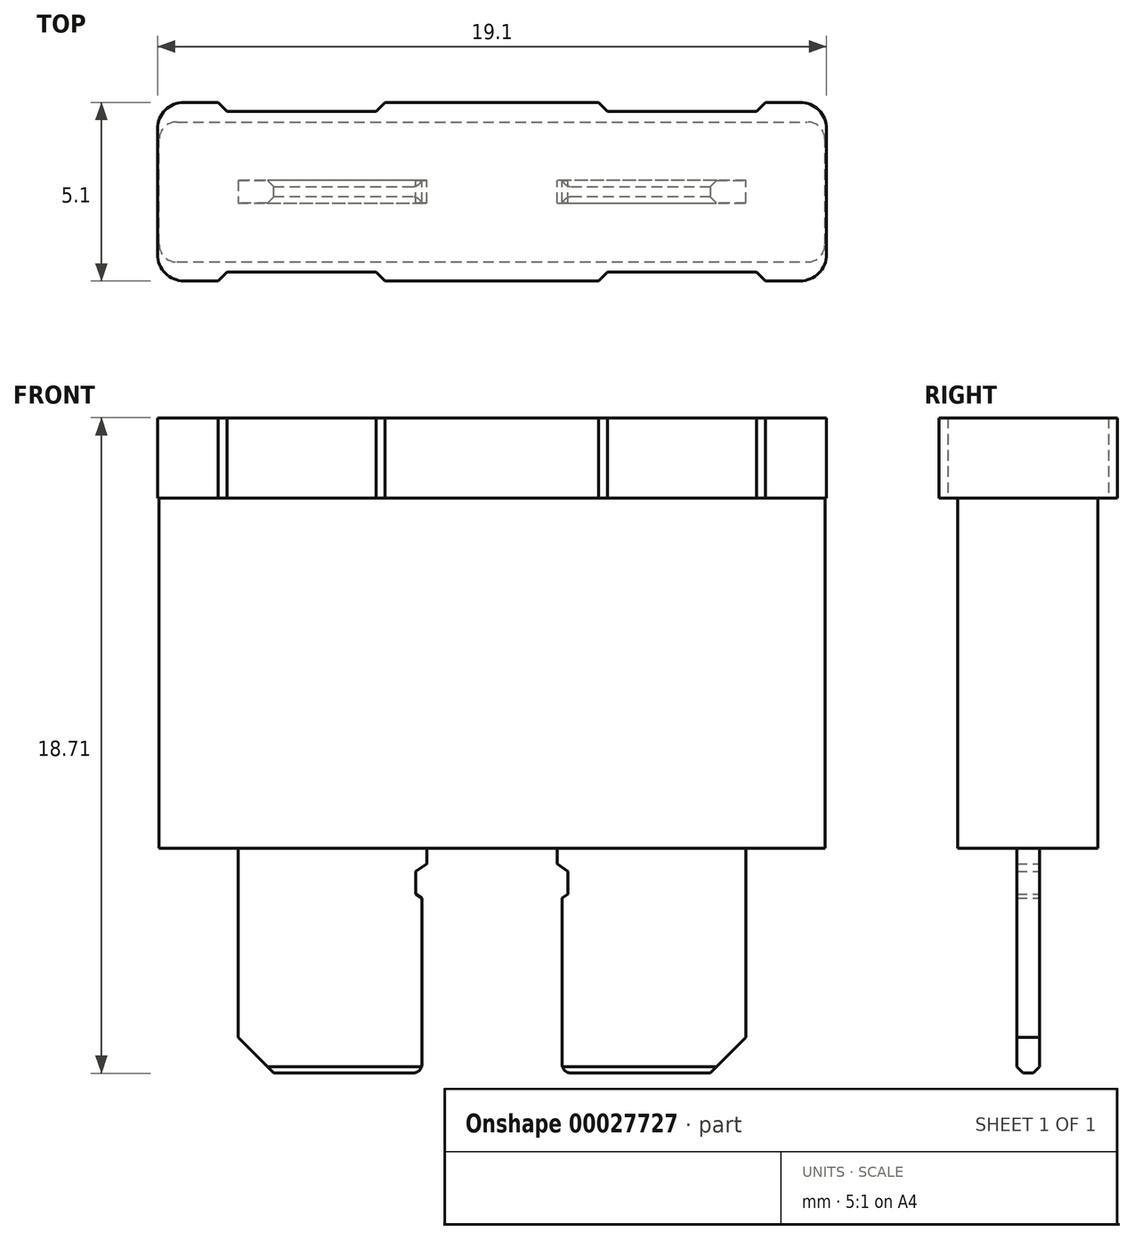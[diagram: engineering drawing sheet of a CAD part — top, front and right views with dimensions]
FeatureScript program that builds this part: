
annotation { "Feature Type Name" : "Feature", "Feature Type Description" : "" }
export const myFeature = defineFeature(function(context is Context, id is Id, definition is map)
    precondition{}
    {
        {
            var Q0;
            Q0=qCreatedBy(makeId("Top.planeOp"),FACE);
            var sketch = newSketch(context, id + "F0", { "sketchPlane" : qUnion([Q0])});
            skLineSegment(sketch, "E0.bottom", {"start": v(-8.79, -2.55) * mm, "end": v(-7.81, -2.55) * mm});
            skLineSegment(sketch, "E0.top", {"start": v(-8.79, 2.55) * mm, "end": v(-7.81, 2.55) * mm});
            skLineSegment(sketch, "E0.left", {"start": v(-9.55, -1.79) * mm, "end": v(-9.55, 1.8) * mm});
            skLineSegment(sketch, "E0.right", {"start": v(9.55, -1.79) * mm, "end": v(9.55, 1.8) * mm});
            skPoint(sketch, "E1.visualSharp", {"position": v(-9.55, 2.55) * mm});
            skArc(sketch, "E1.filletArc", {"start": v(-8.79, 2.55) * mm, "mid": v(-9.33, 2.33) * mm, "end": v(-9.55, 1.8) * mm});
            skPoint(sketch, "E2.visualSharp", {"position": v(-9.55, -2.55) * mm});
            skArc(sketch, "E2.filletArc", {"start": v(-9.55, -1.79) * mm, "mid": v(-9.33, -2.32) * mm, "end": v(-8.79, -2.55) * mm});
            skPoint(sketch, "E3.visualSharp", {"position": v(9.55, -2.55) * mm});
            skArc(sketch, "E3.filletArc", {"start": v(8.79, -2.55) * mm, "mid": v(9.33, -2.32) * mm, "end": v(9.55, -1.79) * mm});
            skPoint(sketch, "E4.visualSharp", {"position": v(9.55, 2.55) * mm});
            skArc(sketch, "E4.filletArc", {"start": v(9.55, 1.8) * mm, "mid": v(9.33, 2.33) * mm, "end": v(8.79, 2.55) * mm});
            skLineSegment(sketch, "E5.0", {"start": v(-7.81, 2.3) * mm, "end": v(-3.05, 2.3) * mm});
            skLineSegment(sketch, "E6.0", {"start": v(-7.81, -2.3) * mm, "end": v(-3.05, -2.3) * mm});
            skLineSegment(sketch, "E7", {"start": v(-3.05, 2.55) * mm, "end": v(-3.05, 2.3) * mm});
            skLineSegment(sketch, "E8", {"start": v(0, 2.55) * mm, "end": v(0, -2.55) * mm});
            skLineSegment(sketch, "E9.MirrorCS", {"start": v(3.05, 2.55) * mm, "end": v(3.05, 2.3) * mm});
            skLineSegment(sketch, "E10.0", {"start": v(-7.81, 2.55) * mm, "end": v(-7.81, 2.3) * mm});
            skLineSegment(sketch, "E11.0", {"start": v(7.81, 2.55) * mm, "end": v(7.81, 2.3) * mm});
            skLineSegment(sketch, "E12.trimOffspring", {"start": v(-3.05, 2.55) * mm, "end": v(3.05, 2.55) * mm});
            skLineSegment(sketch, "E13.trimOffspring", {"start": v(7.81, 2.55) * mm, "end": v(8.79, 2.55) * mm});
            skLineSegment(sketch, "E14.trimOffspring", {"start": v(-3.05, -2.55) * mm, "end": v(3.05, -2.55) * mm});
            skLineSegment(sketch, "E15.trimOffspring", {"start": v(7.81, -2.55) * mm, "end": v(8.79, -2.55) * mm});
            skLineSegment(sketch, "E16.trimOffspring", {"start": v(3.05, -2.3) * mm, "end": v(7.81, -2.3) * mm});
            skLineSegment(sketch, "E17.trimOffspring", {"start": v(3.05, 2.3) * mm, "end": v(7.81, 2.3) * mm});
            skLineSegment(sketch, "E18.trimOffspring", {"start": v(-3.05, -2.3) * mm, "end": v(-3.05, -2.55) * mm});
            skLineSegment(sketch, "E19.trimOffspring", {"start": v(3.05, -2.3) * mm, "end": v(3.05, -2.55) * mm});
            skLineSegment(sketch, "E20.trimOffspring", {"start": v(7.81, -2.3) * mm, "end": v(7.81, -2.55) * mm});
            skLineSegment(sketch, "E21.trimOffspring", {"start": v(-7.81, -2.3) * mm, "end": v(-7.81, -2.55) * mm});
            skSolve(sketch);
        }
        {
            var Q0;
            Q0=qSketchRegion(id+"F0",true);
            extrude(context, id + "F1", {"entities" : qUnion([Q0]), "endBound" : BoundingType.SYMMETRIC, "depth" : 2.3 * mm});
        }
        {
            var Q0;
            Q0=qCreatedBy(makeId("Right.planeOp"),FACE);
            var sketch = newSketch(context, id + "F2", { "sketchPlane" : qUnion([Q0])});
            skLineSegment(sketch, "E22.bottom", {"start": v(-2, -11.14) * mm, "end": v(2, -11.14) * mm});
            skLineSegment(sketch, "E22.top", {"start": v(-2, 0) * mm, "end": v(2, 0) * mm});
            skLineSegment(sketch, "E22.left", {"start": v(-2, -11.14) * mm, "end": v(-2, 0) * mm});
            skLineSegment(sketch, "E22.right", {"start": v(2, -11.14) * mm, "end": v(2, 0) * mm});
            skSolve(sketch);
        }
        {
            var Q0;
            Q0=qSketchRegion(id+"F2",true);
            extrude(context, id + "F3", {"entities" : qUnion([Q0]), "operationType" : NewBodyOperationType.ADD, "endBound" : BoundingType.SYMMETRIC, "depth" : 19 * mm});
        }
        {
            var Q0;
            Q0=makeQuery(id+"F3.opExtrude","CAP_EDGE",EDGE,{"disambiguationData":[OSD([sQuery(id+"F2.wireOp",EDGE,"E22.left")])],"isStart":true});
            var Q1;
            Q1=makeQuery(id+"F3.opExtrude","CAP_EDGE",EDGE,{"disambiguationData":[OSD([sQuery(id+"F2.wireOp",EDGE,"E22.right")])],"isStart":true});
            var Q2;
            Q2=makeQuery(id+"F3.opExtrude","CAP_EDGE",EDGE,{"disambiguationData":[OSD([sQuery(id+"F2.wireOp",EDGE,"E22.left")])],"isStart":false});
            var Q3;
            Q3=makeQuery(id+"F3.opExtrude","CAP_EDGE",EDGE,{"disambiguationData":[OSD([sQuery(id+"F2.wireOp",EDGE,"E22.right")])],"isStart":false});
            fillet(context, id + "F4", {"entities" : qUnion([Q0, Q1, Q2, Q3]), "radius" : 0.5 * mm, "tangentPropagation" : true, "allowEdgeOverflow" : false});
        }
        {
            var Q0;
            Q0=makeQuery(id+"F1.opExtrude","SWEPT_EDGE",EDGE,{"disambiguationData":[OSD([sQuery(id+"F0.wireOp",EDGE,"E5.0"),sQuery(id+"F0.wireOp",EDGE,"E10.0")])]});
            var Q1;
            Q1=makeQuery(id+"F1.opExtrude","SWEPT_EDGE",EDGE,{"disambiguationData":[OSD([sQuery(id+"F0.wireOp",EDGE,"E5.0"),sQuery(id+"F0.wireOp",EDGE,"E7")])]});
            var Q2;
            Q2=makeQuery(id+"F1.opExtrude","SWEPT_EDGE",EDGE,{"disambiguationData":[OSD([sQuery(id+"F0.wireOp",EDGE,"E6.0"),sQuery(id+"F0.wireOp",EDGE,"E18.trimOffspring")])]});
            var Q3;
            Q3=makeQuery(id+"F1.opExtrude","SWEPT_EDGE",EDGE,{"disambiguationData":[OSD([sQuery(id+"F0.wireOp",EDGE,"E6.0"),sQuery(id+"F0.wireOp",EDGE,"E21.trimOffspring")])]});
            var Q4;
            Q4=makeQuery(id+"F1.opExtrude","SWEPT_EDGE",EDGE,{"disambiguationData":[OSD([sQuery(id+"F0.wireOp",EDGE,"E16.trimOffspring"),sQuery(id+"F0.wireOp",EDGE,"E19.trimOffspring")])]});
            var Q5;
            Q5=makeQuery(id+"F1.opExtrude","SWEPT_EDGE",EDGE,{"disambiguationData":[OSD([sQuery(id+"F0.wireOp",EDGE,"E16.trimOffspring"),sQuery(id+"F0.wireOp",EDGE,"E20.trimOffspring")])]});
            var Q6;
            Q6=makeQuery(id+"F1.opExtrude","SWEPT_EDGE",EDGE,{"disambiguationData":[OSD([sQuery(id+"F0.wireOp",EDGE,"E11.0"),sQuery(id+"F0.wireOp",EDGE,"E17.trimOffspring")])]});
            var Q7;
            Q7=makeQuery(id+"F1.opExtrude","SWEPT_EDGE",EDGE,{"disambiguationData":[OSD([sQuery(id+"F0.wireOp",EDGE,"E9.MirrorCS"),sQuery(id+"F0.wireOp",EDGE,"E17.trimOffspring")])]});
            chamfer(context, id + "F5", {"entities" : qUnion([Q0, Q1, Q2, Q3, Q4, Q5, Q6, Q7]), "width" : 0.25 * mm, "tangentPropagation" : true});
        }
        {
            var Q0;
            Q0=makeQuery(id+"F3.opExtrude","SWEPT_FACE",FACE,{"disambiguationData":[OSD([sQuery(id+"F2.wireOp",EDGE,"E22.bottom")])]});
            var sketch = newSketch(context, id + "F6", { "sketchPlane" : qUnion([Q0])});
            skLineSegment(sketch, "E23.bottom", {"start": v(0, 0) * mm, "end": v(10.18, 0) * mm, "construction": true});
            skLineSegment(sketch, "E23.top", {"start": v(0, 0) * mm, "end": v(10.18, 0) * mm, "construction": true});
            skLineSegment(sketch, "E23.left", {"start": v(0, 0) * mm, "end": v(0, 0) * mm});
            skLineSegment(sketch, "E23.right", {"start": v(10.18, 0) * mm, "end": v(10.18, 0) * mm});
            skLineSegment(sketch, "E24", {"start": v(7.25, -0.33) * mm, "end": v(-7.25, -0.33) * mm});
            skLineSegment(sketch, "E25", {"start": v(-7.25, -0.33) * mm, "end": v(-7.25, 0.32) * mm});
            skLineSegment(sketch, "E26", {"start": v(-7.25, 0.32) * mm, "end": v(7.25, 0.32) * mm});
            skLineSegment(sketch, "E27", {"start": v(7.25, 0.32) * mm, "end": v(7.25, -0.33) * mm});
            skSolve(sketch);
        }
        {
            var Q0;
            Q0=qSketchRegion(id+"F6",true);
            extrude(context, id + "F7", {"entities" : qUnion([Q0]), "operationType" : NewBodyOperationType.ADD, "depth" : 6.42 * mm});
        }
        {
            var Q0;
            Q0=makeQuery(id+"F7.opExtrude","CAP_EDGE",EDGE,{"disambiguationData":[OSD([sQuery(id+"F6.wireOp",EDGE,"E25")])],"isStart":false});
            var Q1;
            Q1=makeQuery(id+"F7.opExtrude","CAP_EDGE",EDGE,{"disambiguationData":[OSD([sQuery(id+"F6.wireOp",EDGE,"E27")])],"isStart":false});
            chamfer(context, id + "F8", {"entities" : qUnion([Q0, Q1]), "width" : 1.02 * mm, "tangentPropagation" : true});
        }
        {
            var Q0;
            Q0=makeQuery(id+"F7.opExtrude","CAP_EDGE",EDGE,{"disambiguationData":[OSD([sQuery(id+"F6.wireOp",EDGE,"E26")])],"isStart":false});
            var Q1;
            Q1=makeQuery(id+"F7.opExtrude","CAP_EDGE",EDGE,{"disambiguationData":[OSD([sQuery(id+"F6.wireOp",EDGE,"E24")])],"isStart":false});
            chamfer(context, id + "F9", {"entities" : qUnion([Q0, Q1]), "width" : 0.18 * mm, "tangentPropagation" : true});
        }
        {
            var Q0;
            Q0=makeQuery(id+"F7.opExtrude","SWEPT_FACE",FACE,{"disambiguationData":[OSD([sQuery(id+"F6.wireOp",EDGE,"E24")])]});
            var sketch = newSketch(context, id + "F10", { "sketchPlane" : qUnion([Q0])});
            skLineSegment(sketch, "E28", {"start": v(-2, -17.6) * mm, "end": v(-2, -12.56) * mm});
            skLineSegment(sketch, "E29", {"start": v(-2, -12.56) * mm, "end": v(-2.17, -12.44) * mm});
            skLineSegment(sketch, "E30", {"start": v(-2.17, -12.44) * mm, "end": v(-2.17, -11.8) * mm});
            skLineSegment(sketch, "E31", {"start": v(-2.17, -11.8) * mm, "end": v(-1.86, -11.58) * mm});
            skLineSegment(sketch, "E32", {"start": v(-1.86, -11.58) * mm, "end": v(-1.86, -11.14) * mm});
            skLineSegment(sketch, "E33", {"start": v(0, -17.6) * mm, "end": v(-2, -17.6) * mm, "construction": true});
            skPoint(sketch, "E34.orphan", {"position": v(-2, -18.43) * mm});
            skLineSegment(sketch, "E35", {"start": v(0, -17.6) * mm, "end": v(0, -11.14) * mm, "construction": true});
            skLineSegment(sketch, "E36.MirrorCS", {"start": v(2, -17.6) * mm, "end": v(2, -12.56) * mm});
            skLineSegment(sketch, "E37.MirrorCS", {"start": v(2.17, -12.44) * mm, "end": v(2.17, -11.8) * mm});
            skLineSegment(sketch, "E38.MirrorCS", {"start": v(2.17, -11.8) * mm, "end": v(1.86, -11.58) * mm});
            skLineSegment(sketch, "E39.MirrorCS", {"start": v(1.86, -11.58) * mm, "end": v(1.86, -11.14) * mm});
            skLineSegment(sketch, "E40.MirrorCS", {"start": v(2, -12.56) * mm, "end": v(2.17, -12.44) * mm});
            skLineSegment(sketch, "E41", {"start": v(-2, -17.6) * mm, "end": v(2, -17.6) * mm});
            skLineSegment(sketch, "E42", {"start": v(-1.86, -11.14) * mm, "end": v(1.86, -11.14) * mm});
            skSolve(sketch);
        }
        {
            var Q0;
            Q0=qSketchRegion(id+"F10",true);
            extrude(context, id + "F11", {"entities" : qUnion([Q0]), "operationType" : NewBodyOperationType.REMOVE, "endBound" : BoundingType.THROUGH_ALL, "oppositeDirection" : true, "depth" : 25.4 * mm});
        }
        {
            var Q0;
            Q0=makeQuery(id+"F11.boolean.opBoolean","INTERSECT",EDGE,{"derivedFrom":[makeQuery(id+"F7.opExtrude","CAP_FACE",FACE,{"disambiguationData":[OSD([sQuery(id+"F6.wireOp",EDGE,"E24"),sQuery(id+"F6.wireOp",EDGE,"E25"),sQuery(id+"F6.wireOp",EDGE,"E26"),sQuery(id+"F6.wireOp",EDGE,"E27")])],"isStart":false}),makeQuery(id+"F11.opExtrude","SWEPT_FACE",FACE,{"disambiguationData":[OSD([sQuery(id+"F10.wireOp",EDGE,"E28")])]})]});
            var Q1;
            Q1=makeQuery(id+"F11.boolean.opBoolean","INTERSECT",EDGE,{"derivedFrom":[makeQuery(id+"F7.opExtrude","CAP_FACE",FACE,{"disambiguationData":[OSD([sQuery(id+"F6.wireOp",EDGE,"E24"),sQuery(id+"F6.wireOp",EDGE,"E25"),sQuery(id+"F6.wireOp",EDGE,"E26"),sQuery(id+"F6.wireOp",EDGE,"E27")])],"isStart":false}),makeQuery(id+"F11.opExtrude","SWEPT_FACE",FACE,{"disambiguationData":[OSD([sQuery(id+"F10.wireOp",EDGE,"E36.MirrorCS")])]})]});
            fillet(context, id + "F12", {"entities" : qUnion([Q0, Q1]), "radius" : 0.25 * mm, "tangentPropagation" : true, "allowEdgeOverflow" : false});
        }
    });
